FCSTD DOCUMENT  (FreeCAD 1.0R39109 (Git))
Label: TopDownReference
License: All rights reserved
LicenseURL: https://en.wikipedia.org/wiki/All_rights_reserved
objects: Sketcher::SketchObject×1, PartDesign::Body×1
note: 3 computed .brp shape members not serialized (recipe doc carries the construction recipe); baked Part::Feature solids carry a one-line shape summary decoded from their .brp

FEATURE [Sketcher::SketchObject] Sketch
  ArcFitTolerance = 1e-06
  AttachmentSupport = -> [XY_Plane]
  FullyConstrained = false
  MakeInternals = false
  MapMode = 5
  sketch-geometry (140):
    g0: LineSegment StartX=-198 StartY=178 StartZ=0 EndX=-198 EndY=-178 EndZ=0
    g1: LineSegment StartX=-198 StartY=-178 StartZ=0 EndX=-178 EndY=-178 EndZ=0
    g2: LineSegment StartX=-178 StartY=-178 StartZ=0 EndX=-178 EndY=178 EndZ=0
    g3: LineSegment StartX=-178 StartY=178 StartZ=0 EndX=-198 EndY=178 EndZ=0
    g4: LineSegment StartX=178 StartY=178 StartZ=0 EndX=178 EndY=-178 EndZ=0
    g5: LineSegment StartX=178 StartY=-178 StartZ=0 EndX=198 EndY=-178 EndZ=0
    g6: LineSegment StartX=198 StartY=-178 StartZ=0 EndX=198 EndY=178 EndZ=0
    g7: LineSegment StartX=198 StartY=178 StartZ=0 EndX=178 EndY=178 EndZ=0
    g8: LineSegment StartX=-165 StartY=-54.5269 StartZ=0 EndX=-165 EndY=-64.5269 EndZ=0
    g9: LineSegment StartX=-165 StartY=-64.5269 StartZ=0 EndX=165 EndY=-64.5269 EndZ=0
    g10: LineSegment StartX=165 StartY=-64.5269 StartZ=0 EndX=165 EndY=-54.5269 EndZ=0
    g11: LineSegment StartX=165 StartY=-54.5269 StartZ=0 EndX=-165 EndY=-54.5269 EndZ=0
    g12: LineSegment StartX=-178 StartY=198 StartZ=0 EndX=-178 EndY=178 EndZ=0
    g13: LineSegment StartX=-178 StartY=178 StartZ=0 EndX=178 EndY=178 EndZ=0
    g14: LineSegment StartX=178 StartY=178 StartZ=0 EndX=178 EndY=198 EndZ=0
    g15: LineSegment StartX=178 StartY=198 StartZ=0 EndX=-178 EndY=198 EndZ=0
    g16: LineSegment StartX=-178 StartY=-178 StartZ=0 EndX=-178 EndY=-198 EndZ=0
    g17: LineSegment StartX=-178 StartY=-198 StartZ=0 EndX=178 EndY=-198 EndZ=0
    g18: LineSegment StartX=178 StartY=-198 StartZ=0 EndX=178 EndY=-178 EndZ=0
    g19: LineSegment StartX=178 StartY=-178 StartZ=0 EndX=-178 EndY=-178 EndZ=0
    g20: LineSegment StartX=-38.3157 StartY=165 StartZ=0 EndX=-38.3157 EndY=-165 EndZ=0
    g21: LineSegment StartX=-38.3157 StartY=-165 StartZ=0 EndX=-28.3157 EndY=-165 EndZ=0
    g22: LineSegment StartX=-28.3157 StartY=-165 StartZ=0 EndX=-28.3157 EndY=165 EndZ=0
    g23: LineSegment StartX=-28.3157 StartY=165 StartZ=0 EndX=-38.3157 EndY=165 EndZ=0
    g24: LineSegment StartX=-28.3157 StartY=150 StartZ=0 EndX=-28.3157 EndY=-150 EndZ=0
    g25: LineSegment StartX=-28.3157 StartY=-150 StartZ=0 EndX=-21.8157 EndY=-150 EndZ=0
    g26: LineSegment StartX=-21.8157 StartY=-150 StartZ=0 EndX=-21.8157 EndY=150 EndZ=0
    g27: LineSegment StartX=-21.8157 StartY=150 StartZ=0 EndX=-28.3157 EndY=150 EndZ=0
    g28: LineSegment StartX=-150 StartY=-64.5269 StartZ=0 EndX=-150 EndY=-71.0269 EndZ=0
    g29: LineSegment StartX=-150 StartY=-71.0269 StartZ=0 EndX=150 EndY=-71.0269 EndZ=0
    g30: LineSegment StartX=150 StartY=-71.0269 StartZ=0 EndX=150 EndY=-64.5269 EndZ=0
    g31: LineSegment StartX=150 StartY=-64.5269 StartZ=0 EndX=-150 EndY=-64.5269 EndZ=0
    g32: Circle CenterX=184.1 CenterY=-219.15 CenterZ=0 NormalX=0 NormalY=0 NormalZ=1 AngleXU=0 Radius=19.1
    g33: LineSegment StartX=-178 StartY=165 StartZ=0 EndX=-178 EndY=-165 EndZ=0
    g34: LineSegment StartX=-178 StartY=-165 StartZ=0 EndX=-170 EndY=-165 EndZ=0
    g35: LineSegment StartX=-170 StartY=-165 StartZ=0 EndX=-170 EndY=165 EndZ=0
    g36: LineSegment StartX=-170 StartY=165 StartZ=0 EndX=-178 EndY=165 EndZ=0
    g37: LineSegment StartX=-165 StartY=-178 StartZ=0 EndX=165 EndY=-178 EndZ=0
    g38: LineSegment StartX=165 StartY=-178 StartZ=0 EndX=165 EndY=-170 EndZ=0
    g39: LineSegment StartX=165 StartY=-170 StartZ=0 EndX=-165 EndY=-170 EndZ=0
    g40: LineSegment StartX=-165 StartY=-170 StartZ=0 EndX=-165 EndY=-178 EndZ=0
    g41: LineSegment StartX=178 StartY=-165 StartZ=0 EndX=178 EndY=165 EndZ=0
    g42: LineSegment StartX=178 StartY=165 StartZ=0 EndX=170 EndY=165 EndZ=0
    g43: LineSegment StartX=170 StartY=165 StartZ=0 EndX=170 EndY=-165 EndZ=0
    g44: LineSegment StartX=170 StartY=-165 StartZ=0 EndX=178 EndY=-165 EndZ=0
    g45: LineSegment StartX=165 StartY=178 StartZ=0 EndX=-165 EndY=178 EndZ=0
    g46: LineSegment StartX=-165 StartY=178 StartZ=0 EndX=-165 EndY=170 EndZ=0
    g47: LineSegment StartX=-165 StartY=170 StartZ=0 EndX=165 EndY=170 EndZ=0
    g48: LineSegment StartX=165 StartY=170 StartZ=0 EndX=165 EndY=178 EndZ=0
    g49: LineSegment StartX=-198 StartY=178 StartZ=0 EndX=-178 EndY=178 EndZ=0
    g50: LineSegment StartX=-178 StartY=178 StartZ=0 EndX=-178 EndY=198 EndZ=0
    g51: LineSegment StartX=-178 StartY=198 StartZ=0 EndX=-198 EndY=198 EndZ=0
    g52: LineSegment StartX=-198 StartY=198 StartZ=0 EndX=-198 EndY=178 EndZ=0
    g53: LineSegment StartX=-198 StartY=-178 StartZ=0 EndX=-198 EndY=-198 EndZ=0
    g54: LineSegment StartX=-198 StartY=-198 StartZ=0 EndX=-178 EndY=-198 EndZ=0
    g55: LineSegment StartX=-178 StartY=-198 StartZ=0 EndX=-178 EndY=-178 EndZ=0
    g56: LineSegment StartX=-178 StartY=-178 StartZ=0 EndX=-198 EndY=-178 EndZ=0
    g57: LineSegment StartX=178 StartY=-198 StartZ=0 EndX=198 EndY=-198 EndZ=0
    g58: LineSegment StartX=198 StartY=-198 StartZ=0 EndX=198 EndY=-178 EndZ=0
    g59: LineSegment StartX=198 StartY=-178 StartZ=0 EndX=178 EndY=-178 EndZ=0
    g60: LineSegment StartX=178 StartY=-178 StartZ=0 EndX=178 EndY=-198 EndZ=0
    g61: LineSegment StartX=198 StartY=178 StartZ=0 EndX=198 EndY=198 EndZ=0
    g62: LineSegment StartX=198 StartY=198 StartZ=0 EndX=178 EndY=198 EndZ=0
    g63: LineSegment StartX=178 StartY=198 StartZ=0 EndX=178 EndY=178 EndZ=0
    g64: LineSegment StartX=178 StartY=178 StartZ=0 EndX=198 EndY=178 EndZ=0
    g65: LineSegment StartX=162.95 StartY=-198 StartZ=0 EndX=162.95 EndY=-240.3 EndZ=0
    g66: LineSegment StartX=162.95 StartY=-240.3 StartZ=0 EndX=205.25 EndY=-240.3 EndZ=0
    g67: LineSegment StartX=205.25 StartY=-240.3 StartZ=0 EndX=205.25 EndY=-198 EndZ=0
    g68: LineSegment StartX=205.25 StartY=-198 StartZ=0 EndX=162.95 EndY=-198 EndZ=0
    g69: GeomPoint [constr] X=184.1 Y=-219.15 Z=0
    g70: Circle CenterX=-184.1 CenterY=219.15 CenterZ=0 NormalX=0 NormalY=0 NormalZ=1 AngleXU=0 Radius=19.1
    g71: LineSegment StartX=-205.25 StartY=240.3 StartZ=0 EndX=-205.25 EndY=198 EndZ=0
    g72: LineSegment StartX=-205.25 StartY=198 StartZ=0 EndX=-162.95 EndY=198 EndZ=0
    g73: LineSegment StartX=-162.95 StartY=198 StartZ=0 EndX=-162.95 EndY=240.3 EndZ=0
    g74: LineSegment StartX=-162.95 StartY=240.3 StartZ=0 EndX=-205.25 EndY=240.3 EndZ=0
    g75: GeomPoint [constr] X=-184.1 Y=219.15 Z=0
    g76: Circle CenterX=219.15 CenterY=184.1 CenterZ=0 NormalX=0 NormalY=0 NormalZ=1 AngleXU=0 Radius=19.1
    g77: LineSegment StartX=198 StartY=162.95 StartZ=0 EndX=198 EndY=205.25 EndZ=0
    g78: LineSegment StartX=198 StartY=205.25 StartZ=0 EndX=240.3 EndY=205.25 EndZ=0
    g79: LineSegment StartX=240.3 StartY=205.25 StartZ=0 EndX=240.3 EndY=162.95 EndZ=0
    g80: LineSegment StartX=240.3 StartY=162.95 StartZ=0 EndX=198 EndY=162.95 EndZ=0
    g81: GeomPoint [constr] X=219.15 Y=184.1 Z=0
    g82: Circle CenterX=-219.15 CenterY=-184.1 CenterZ=0 NormalX=0 NormalY=0 NormalZ=1 AngleXU=0 Radius=19.1
    g83: LineSegment StartX=-198 StartY=-162.95 StartZ=0 EndX=-198 EndY=-205.25 EndZ=0
    g84: LineSegment StartX=-198 StartY=-205.25 StartZ=0 EndX=-240.3 EndY=-205.25 EndZ=0
    g85: LineSegment StartX=-240.3 StartY=-205.25 StartZ=0 EndX=-240.3 EndY=-162.95 EndZ=0
    g86: LineSegment StartX=-240.3 StartY=-162.95 StartZ=0 EndX=-198 EndY=-162.95 EndZ=0
    g87: GeomPoint [constr] X=-219.15 Y=-184.1 Z=0
    g88: LineSegment StartX=-55.8157 StartY=-165 StartZ=0 EndX=-55.8157 EndY=-175 EndZ=0
    g89: LineSegment StartX=-55.8157 StartY=-175 StartZ=0 EndX=-10.8157 EndY=-175 EndZ=0
    g90: LineSegment StartX=-10.8157 StartY=-175 StartZ=0 EndX=-10.8157 EndY=-165 EndZ=0
    g91: LineSegment StartX=-10.8157 StartY=-165 StartZ=0 EndX=-55.8157 EndY=-165 EndZ=0
    g92: LineSegment StartX=165 StartY=-37.0269 StartZ=0 EndX=165 EndY=-82.0269 EndZ=0
    g93: LineSegment StartX=165 StartY=-82.0269 StartZ=0 EndX=175 EndY=-82.0269 EndZ=0
    g94: LineSegment StartX=175 StartY=-82.0269 StartZ=0 EndX=175 EndY=-37.0269 EndZ=0
    g95: LineSegment StartX=175 StartY=-37.0269 StartZ=0 EndX=165 EndY=-37.0269 EndZ=0
    g96: LineSegment StartX=-175 StartY=-37.0269 StartZ=0 EndX=-175 EndY=-82.0269 EndZ=0
    g97: LineSegment StartX=-175 StartY=-82.0269 StartZ=0 EndX=-165 EndY=-82.0269 EndZ=0
    g98: LineSegment StartX=-165 StartY=-82.0269 StartZ=0 EndX=-165 EndY=-37.0269 EndZ=0
    g99: LineSegment StartX=-165 StartY=-37.0269 StartZ=0 EndX=-175 EndY=-37.0269 EndZ=0
    g100: LineSegment StartX=-55.8157 StartY=175 StartZ=0 EndX=-55.8157 EndY=165 EndZ=0
    g101: LineSegment StartX=-55.8157 StartY=165 StartZ=0 EndX=-10.8157 EndY=165 EndZ=0
    g102: LineSegment StartX=-10.8157 StartY=165 StartZ=0 EndX=-10.8157 EndY=175 EndZ=0
    g103: LineSegment StartX=-10.8157 StartY=175 StartZ=0 EndX=-55.8157 EndY=175 EndZ=0
    g104: LineSegment [constr] StartX=165 StartY=-170 StartZ=0 EndX=170 EndY=-165 EndZ=0
    g105: LineSegment [constr] StartX=165 StartY=170 StartZ=0 EndX=170 EndY=165 EndZ=0
    g106: LineSegment [constr] StartX=-165 StartY=170 StartZ=0 EndX=-170 EndY=165 EndZ=0
    g107: LineSegment [constr] StartX=-170 StartY=-165 StartZ=0 EndX=-165 EndY=-170 EndZ=0
    g108: ArcOfCircle CenterX=184.1 CenterY=218 CenterZ=0 NormalX=0 NormalY=0 NormalZ=1 AngleXU=0 Radius=17.1 StartAngle=0 EndAngle=3.14159
    g109: ArcOfCircle CenterX=184.1 CenterY=-219.15 CenterZ=0 NormalX=0 NormalY=0 NormalZ=1 AngleXU=0 Radius=17.1 StartAngle=3.14159 EndAngle=6.28319
    g110: LineSegment StartX=201.2 StartY=218 StartZ=0 EndX=201.2 EndY=-219.15 EndZ=0
    g111: LineSegment StartX=167 StartY=218 StartZ=0 EndX=167 EndY=-219.15 EndZ=0
    g112: ArcOfCircle CenterX=184.1 CenterY=218 CenterZ=0 NormalX=0 NormalY=0 NormalZ=1 AngleXU=0 Radius=19.1 StartAngle=0 EndAngle=3.14159
    g113: ArcOfCircle CenterX=184.1 CenterY=-219.15 CenterZ=0 NormalX=0 NormalY=0 NormalZ=1 AngleXU=0 Radius=19.1 StartAngle=3.14159 EndAngle=6.28319
    g114: LineSegment StartX=203.2 StartY=218 StartZ=0 EndX=203.2 EndY=-219.15 EndZ=0
    g115: LineSegment StartX=165 StartY=218 StartZ=0 EndX=165 EndY=-219.15 EndZ=0
    g116: ArcOfCircle CenterX=-218 CenterY=184.1 CenterZ=0 NormalX=0 NormalY=0 NormalZ=1 AngleXU=0 Radius=19.1 StartAngle=1.5708 EndAngle=4.71239
    g117: ArcOfCircle CenterX=219.15 CenterY=184.1 CenterZ=0 NormalX=0 NormalY=0 NormalZ=1 AngleXU=0 Radius=19.1 StartAngle=4.71239 EndAngle=7.85398
    g118: LineSegment StartX=-218 StartY=203.2 StartZ=0 EndX=219.15 EndY=203.2 EndZ=0
    g119: LineSegment StartX=-218 StartY=165 StartZ=0 EndX=219.15 EndY=165 EndZ=0
    g120: ArcOfCircle CenterX=-218 CenterY=184.1 CenterZ=0 NormalX=0 NormalY=0 NormalZ=1 AngleXU=0 Radius=17.1 StartAngle=1.5708 EndAngle=4.71239
    g121: ArcOfCircle CenterX=219.15 CenterY=184.1 CenterZ=0 NormalX=0 NormalY=0 NormalZ=1 AngleXU=0 Radius=17.1 StartAngle=4.71239 EndAngle=7.85398
    g122: LineSegment StartX=-218 StartY=201.2 StartZ=0 EndX=219.15 EndY=201.2 EndZ=0
    g123: LineSegment StartX=-218 StartY=167 StartZ=0 EndX=219.15 EndY=167 EndZ=0
    g124: ArcOfCircle CenterX=-219.15 CenterY=-184.1 CenterZ=0 NormalX=0 NormalY=0 NormalZ=1 AngleXU=0 Radius=17.1 StartAngle=1.5708 EndAngle=4.71239
    g125: ArcOfCircle CenterX=218 CenterY=-184.1 CenterZ=0 NormalX=0 NormalY=0 NormalZ=1 AngleXU=0 Radius=17.1 StartAngle=4.71239 EndAngle=7.85398
    g126: LineSegment StartX=-219.15 StartY=-167 StartZ=0 EndX=218 EndY=-167 EndZ=0
    g127: LineSegment StartX=-219.15 StartY=-201.2 StartZ=0 EndX=218 EndY=-201.2 EndZ=0
    g128: ArcOfCircle CenterX=-219.15 CenterY=-184.1 CenterZ=0 NormalX=0 NormalY=0 NormalZ=1 AngleXU=0 Radius=19.1 StartAngle=1.5708 EndAngle=4.71239
    g129: ArcOfCircle CenterX=218 CenterY=-184.1 CenterZ=0 NormalX=0 NormalY=0 NormalZ=1 AngleXU=0 Radius=19.1 StartAngle=4.71239 EndAngle=7.85398
    g130: LineSegment StartX=-219.15 StartY=-165 StartZ=0 EndX=218 EndY=-165 EndZ=0
    g131: LineSegment StartX=-219.15 StartY=-203.2 StartZ=0 EndX=218 EndY=-203.2 EndZ=0
    g132: ArcOfCircle CenterX=-184.1 CenterY=219.15 CenterZ=0 NormalX=0 NormalY=0 NormalZ=1 AngleXU=0 Radius=17.1 StartAngle=0 EndAngle=3.14159
    g133: ArcOfCircle CenterX=-184.1 CenterY=-218 CenterZ=0 NormalX=0 NormalY=0 NormalZ=1 AngleXU=0 Radius=17.1 StartAngle=3.14159 EndAngle=6.28319
    g134: LineSegment StartX=-167 StartY=219.15 StartZ=0 EndX=-167 EndY=-218 EndZ=0
    g135: LineSegment StartX=-201.2 StartY=219.15 StartZ=0 EndX=-201.2 EndY=-218 EndZ=0
    g136: ArcOfCircle CenterX=-184.1 CenterY=219.15 CenterZ=0 NormalX=0 NormalY=0 NormalZ=1 AngleXU=0 Radius=19.1 StartAngle=2e-16 EndAngle=3.14159
    g137: ArcOfCircle CenterX=-184.1 CenterY=-218 CenterZ=0 NormalX=0 NormalY=0 NormalZ=1 AngleXU=0 Radius=19.1 StartAngle=3.14159 EndAngle=6.28319
    g138: LineSegment StartX=-165 StartY=219.15 StartZ=0 EndX=-165 EndY=-218 EndZ=0
    g139: LineSegment StartX=-203.2 StartY=219.15 StartZ=0 EndX=-203.2 EndY=-218 EndZ=0
  constraints (361):
    c: Coincident(g0,g1)
    c: Coincident(g1,g2)
    c: Coincident(g2,g3)
    c: Coincident(g3,g0)
    c: Vertical(g0)
    c: Vertical(g2)
    c: Horizontal(g1)
    c: Horizontal(g3)
    c: Coincident(g4,g5)
    c: Coincident(g5,g6)
    c: Coincident(g6,g7)
    c: Coincident(g7,g4)
    c: Vertical(g4)
    c: Vertical(g6)
    c: Horizontal(g5)
    c: Horizontal(g7)
    c: Coincident(g8,g9)
    c: Coincident(g9,g10)
    c: Coincident(g10,g11)
    c: Coincident(g11,g8)
    c: Vertical(g8)
    c: Vertical(g10)
    c: Horizontal(g9)
    c: Horizontal(g11)
    c: Coincident(g12,g13)
    c: Coincident(g13,g14)
    c: Coincident(g14,g15)
    c: Coincident(g15,g12)
    c: Vertical(g12)
    c: Vertical(g14)
    c: Horizontal(g13)
    c: Horizontal(g15)
    c: Coincident(g16,g17)
    c: Coincident(g17,g18)
    c: Coincident(g18,g19)
    c: Coincident(g19,g16)
    c: Vertical(g16)
    c: Vertical(g18)
    c: Horizontal(g17)
    c: Horizontal(g19)
    c: Coincident(g20,g21)
    c: Coincident(g21,g22)
    c: Coincident(g22,g23)
    c: Coincident(g23,g20)
    c: Vertical(g20)
    c: Vertical(g22)
    c: Horizontal(g21)
    c: Horizontal(g23)
    c: Coincident(g24,g25)
    c: Coincident(g25,g26)
    c: Coincident(g26,g27)
    c: Coincident(g27,g24)
    c: Vertical(g24)
    c: Vertical(g26)
    c: Horizontal(g25)
    c: Horizontal(g27)
    c: PointOnObject(g24,g22)
    c: Coincident(g28,g29)
    c: Coincident(g29,g30)
    c: Coincident(g30,g31)
    c: Coincident(g31,g28)
    c: Vertical(g28)
    c: Vertical(g30)
    c: Horizontal(g29)
    c: Horizontal(g31)
    c: PointOnObject(g28,g9)
    c: Equal(g27,g28)
    c: Equal(g23,g8)
    c: Equal(g20,g11)
    c: Distance(g2,g0) = 20
    c: Equal(g3,g7)
    c: Equal(g3,g12)
    c: Equal(g3,g16)
    c: DistanceY(g8,g8) = 10
    c: Distance(g28,g28) = 6.5
    c: DistanceX(g29,g29) = 300
    c: Coincident(g33,g34)
    c: Coincident(g34,g35)
    c: Coincident(g35,g36)
    c: Coincident(g36,g33)
    c: Vertical(g33)
    c: Vertical(g35)
    c: Horizontal(g34)
    c: Horizontal(g36)
    c: Distance(g33,g35) = 8
    c: Distance(g34,g36) = 330
    c: PointOnObject(g33,g2)
    c: Coincident(g37,g38)
    c: Coincident(g38,g39)
    c: Coincident(g39,g40)
    c: Coincident(g40,g37)
    c: Horizontal(g37)
    c: Horizontal(g39)
    c: Vertical(g38)
    c: Vertical(g40)
    c: PointOnObject(g37,g19)
    c: Coincident(g41,g42)
    c: Coincident(g42,g43)
    c: Coincident(g43,g44)
    c: Coincident(g44,g41)
    c: Vertical(g41)
    c: Vertical(g43)
    c: Horizontal(g42)
    c: Horizontal(g44)
    c: PointOnObject(g41,g4)
    c: Coincident(g45,g46)
    c: Coincident(g46,g47)
    c: Coincident(g47,g48)
    c: Coincident(g48,g45)
    c: Horizontal(g45)
    c: Horizontal(g47)
    c: Vertical(g46)
    c: Vertical(g48)
    c: PointOnObject(g45,g13)
    c: Equal(g35,g39)
    c: Equal(g35,g43)
    c: Equal(g35,g47)
    c: Equal(g34,g40)
    c: Equal(g34,g44)
    c: Equal(g34,g48)
    c: Coincident(g49,g50)
    c: Coincident(g50,g51)
    c: Coincident(g51,g52)
    c: Coincident(g52,g49)
    c: Horizontal(g49)
    c: Horizontal(g51)
    c: Vertical(g50)
    c: Vertical(g52)
    c: Coincident(g49,g0)
    c: Coincident(g50,g12)
    c: Coincident(g53,g54)
    c: Coincident(g54,g55)
    c: Coincident(g55,g56)
    c: Coincident(g56,g53)
    c: Vertical(g53)
    c: Vertical(g55)
    c: Horizontal(g54)
    c: Horizontal(g56)
    c: Coincident(g53,g0)
    c: Coincident(g54,g16)
    c: Coincident(g57,g58)
    c: Coincident(g58,g59)
    c: Coincident(g59,g60)
    c: Coincident(g60,g57)
    c: Horizontal(g57)
    c: Horizontal(g59)
    c: Vertical(g58)
    c: Vertical(g60)
    c: Coincident(g57,g17)
    c: Coincident(g58,g5)
    c: Coincident(g61,g62)
    c: Coincident(g62,g63)
    c: Coincident(g63,g64)
    c: Coincident(g64,g61)
    c: Vertical(g61)
    c: Vertical(g63)
    c: Horizontal(g62)
    c: Horizontal(g64)
    c: Coincident(g61,g6)
    c: Coincident(g62,g14)
    c: Coincident(g2,g12)
    c: Coincident(g4,g13)
    c: Coincident(g18,g4)
    c: Coincident(g16,g1)
    c: Coincident(g65,g66)
    c: Coincident(g66,g67)
    c: Coincident(g67,g68)
    c: Coincident(g68,g65)
    c: Vertical(g65)
    c: Vertical(g67)
    c: Horizontal(g66)
    c: Horizontal(g68)
    c: Symmetric(g67,g65,g69)
    c: Coincident(g69,g32)
    c: Equal(g68,g65)
    c: Coincident(g71,g72)
    c: Coincident(g72,g73)
    c: Coincident(g73,g74)
    c: Coincident(g74,g71)
    c: Vertical(g71)
    c: Vertical(g73)
    c: Horizontal(g72)
    c: Horizontal(g74)
    c: Symmetric(g73,g71,g75)
    c: Distance(g71,g73) = 42.3
    c: Coincident(g75,g70)
    c: Equal(g74,g71)
    c: Coincident(g77,g78)
    c: Coincident(g78,g79)
    c: Coincident(g79,g80)
    c: Coincident(g80,g77)
    c: Vertical(g77)
    c: Vertical(g79)
    c: Horizontal(g78)
    c: Horizontal(g80)
    c: Symmetric(g79,g77,g81)
    c: Coincident(g81,g76)
    c: Equal(g80,g77)
    c: Coincident(g83,g84)
    c: Coincident(g84,g85)
    c: Coincident(g85,g86)
    c: Coincident(g86,g83)
    c: Vertical(g83)
    c: Vertical(g85)
    c: Horizontal(g84)
    c: Horizontal(g86)
    c: Symmetric(g85,g83,g87)
    c: Coincident(g87,g82)
    c: Equal(g86,g83)
    c: Equal(g74,g86)
    c: Equal(g74,g68)
    c: Equal(g74,g80)
    c: Equal(g70,g82)
    c: Equal(g70,g32)
    c: Equal(g70,g76)
    c: Coincident(g88,g89)
    c: Coincident(g89,g90)
    c: Coincident(g90,g91)
    c: Coincident(g91,g88)
    c: Vertical(g88)
    c: Vertical(g90)
    c: Horizontal(g89)
    c: Horizontal(g91)
    c: Distance(g90,g88) = 45
    c: Distance(g90,g90) = 10
    c: Coincident(g92,g93)
    c: Coincident(g93,g94)
    c: Coincident(g94,g95)
    c: Coincident(g95,g92)
    c: Vertical(g92)
    c: Vertical(g94)
    c: Horizontal(g93)
    c: Horizontal(g95)
    c: Coincident(g96,g97)
    c: Coincident(g97,g98)
    c: Coincident(g98,g99)
    c: Coincident(g99,g96)
    c: Vertical(g96)
    c: Vertical(g98)
    c: Horizontal(g97)
    c: Horizontal(g99)
    c: Coincident(g100,g101)
    c: Coincident(g101,g102)
    c: Coincident(g102,g103)
    c: Coincident(g103,g100)
    c: Vertical(g100)
    c: Vertical(g102)
    c: Horizontal(g101)
    c: Horizontal(g103)
    c: Equal(g91,g92)
    c: Equal(g92,g101)
    c: Equal(g91,g98)
    c: Equal(g90,g93)
    c: Equal(g90,g97)
    c: Equal(g88,g100)
    c: Distance(g2,g96) = 3
    c: Distance(g4,g94) = 3
    c: Distance(g13,g103) = 3
    c: PointOnObject(g92,g10)
    c: PointOnObject(g8,g98)
    c: PointOnObject(g90,g21)
    c: PointOnObject(g101,g23)
    c: PointOnObject(g39,g46)
    c: PointOnObject(g43,g34)
    c: PointOnObject(g92,g99)
    c: PointOnObject(g101,g90)
    c: Distance(g22,g101) = 17.5
    c: DistanceY(g92,g9) = 17.5
    c: Symmetric(g61,g53,g-1)
    c: DistanceY(g24,g22) = 15
    c: DistanceY(g21,g24) = 15
    c: DistanceX(g8,g28) = 15
    c: DistanceX(g30,g9) = 15
    c: Distance(g19,g89) = 3
    c: Coincident(g104,g38)
    c: Coincident(g104,g43)
    c: Coincident(g105,g47)
    c: Coincident(g105,g42)
    c: Coincident(g106,g46)
    c: Coincident(g106,g35)
    c: Coincident(g107,g34)
    c: Coincident(g107,g39)
    c: Parallel(g107,g105)
    c: Parallel(g104,g106)
    c: Tangent(g108,g110) = 1.5708
    c: Tangent(g108,g111) = -1.5708
    c: Tangent(g109,g110) = 1.5708
    c: Tangent(g109,g111) = -1.5708
    c: Equal(g108,g109)
    c: Vertical(g110)
    c: Tangent(g112,g114) = 1.5708
    c: Tangent(g112,g115) = -1.5708
    c: Tangent(g113,g114) = 1.5708
    c: Tangent(g113,g115) = -1.5708
    c: Equal(g112,g113)
    c: DistanceX(g112,g108) = 2
    c: Coincident(g112,g108)
    c: Coincident(g109,g113)
    c: Tangent(g116,g118) = 1.5708
    c: Tangent(g116,g119) = -1.5708
    c: Tangent(g117,g118) = 1.5708
    c: Tangent(g117,g119) = -1.5708
    c: Equal(g116,g117)
    c: Tangent(g120,g122) = 1.5708
    c: Tangent(g120,g123) = -1.5708
    c: Tangent(g121,g122) = 1.5708
    c: Tangent(g121,g123) = -1.5708
    c: Equal(g120,g121)
    c: Coincident(g120,g116)
    c: Coincident(g117,g121)
    c: Tangent(g124,g126) = 1.5708
    c: Tangent(g124,g127) = -1.5708
    c: Tangent(g125,g126) = 1.5708
    c: Tangent(g125,g127) = -1.5708
    c: Equal(g124,g125)
    c: Tangent(g128,g130) = 1.5708
    c: Tangent(g128,g131) = -1.5708
    c: Tangent(g129,g130) = 1.5708
    c: Tangent(g129,g131) = -1.5708
    c: Equal(g128,g129)
    c: Coincident(g128,g124)
    c: Coincident(g125,g129)
    c: Tangent(g132,g134) = 1.5708
    c: Tangent(g132,g135) = -1.5708
    c: Tangent(g133,g134) = 1.5708
    c: Tangent(g133,g135) = -1.5708
    c: Equal(g132,g133)
    c: Vertical(g134)
    c: Tangent(g136,g138) = 1.5708
    c: Tangent(g136,g139) = -1.5708
    c: Tangent(g137,g138) = 1.5708
    c: Tangent(g137,g139) = -1.5708
    c: Equal(g136,g137)
    c: DistanceX(g136,g132) = 2
    c: Coincident(g136,g132)
    c: Coincident(g133,g137)
    c: Horizontal(g122)
    c: Horizontal(g126)
    c: DistanceY(g124,g128) = 2
    c: DistanceY(g120,g116) = 2
    c: Coincident(g124,g82)
    c: Coincident(g117,g76)
    c: Coincident(g32,g109)
    c: Coincident(g132,g70)
    c: Equal(g130,g119)
    c: Equal(g138,g115)
    c: Equal(g128,g116)
    c: Equal(g116,g136)
    c: Equal(g129,g112)
    c: Distance(g39,g126) = 3
    c: Diameter(g82) = 38.2
    c: Tangent(g82,g130)
    c: Distance(g47,g123) = 3
    c: Distance(g43,g111) = 3
    c: Distance(g35,g134) = 3
    c: PointOnObject(g83,g53)
    c: PointOnObject(g57,g68)
    c: Distance(g125,g6) = 20
    c: Equal(g131,g114)
    c: PointOnObject(g61,g77)
    c: PointOnObject(g51,g72)
FEATURE [PartDesign::Body] Body
  AllowCompound = false
  Group = -> [Sketch]
  Origin = -> Origin
